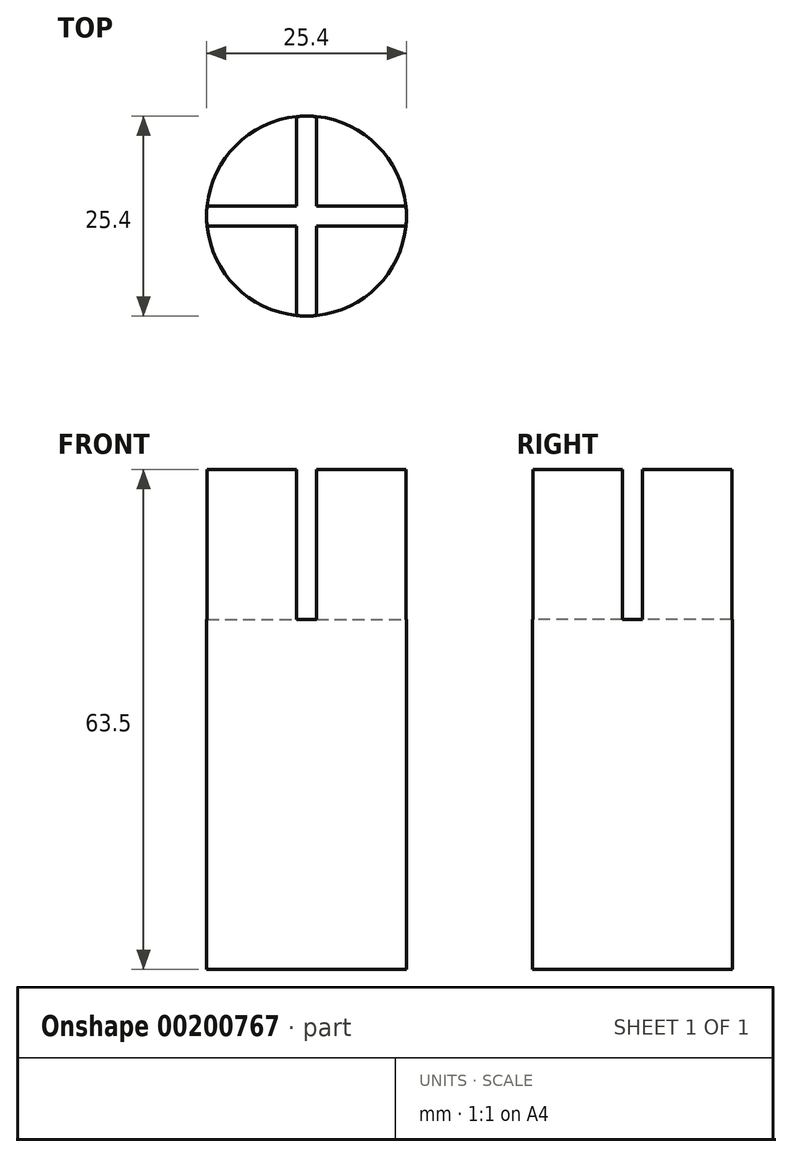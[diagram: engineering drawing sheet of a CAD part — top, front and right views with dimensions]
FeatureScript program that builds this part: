
annotation { "Feature Type Name" : "Feature", "Feature Type Description" : "" }
export const myFeature = defineFeature(function(context is Context, id is Id, definition is map)
    precondition{}
    {
        {
            var Q0;
            Q0=qCreatedBy(makeId("Top.planeOp"),FACE);
            var sketch = newSketch(context, id + "F0", { "sketchPlane" : qUnion([Q0])});
            skCircle(sketch, "E0", {"center": v(0, 0) * mm, "radius": 12.7 * mm});
            skSolve(sketch);
        }
        {
            var Q0;
            Q0 = qSketchRegion(id + "F0", true);
            extrude(context, id + "F1", {"entities" : qUnion([Q0]), "depth" : 63.5 * mm});
        }
        {
            var Q0;
            Q0=makeQuery(id+"F1.opExtrude","CAP_FACE",FACE,{"disambiguationData":[OSD([sQuery(id+"F0.wireOp",EDGE,"E0")])],"isStart":false});
            var sketch = newSketch(context, id + "F2", { "sketchPlane" : qUnion([Q0])});
            skLineSegment(sketch, "E1.bottom", {"start": v(-1.27, 12.7) * mm, "end": v(1.27, 12.7) * mm});
            skLineSegment(sketch, "E1.top", {"start": v(-1.27, -12.7) * mm, "end": v(1.27, -12.7) * mm});
            skLineSegment(sketch, "E1.left", {"start": v(-1.27, 12.7) * mm, "end": v(-1.27, -12.7) * mm});
            skLineSegment(sketch, "E1.right", {"start": v(1.27, 12.7) * mm, "end": v(1.27, -12.7) * mm});
            skPoint(sketch, "E1.middle", {"position": v(0, 0) * mm});
            skLineSegment(sketch, "E2.bottom", {"start": v(-12.7, 1.27) * mm, "end": v(12.7, 1.27) * mm});
            skLineSegment(sketch, "E2.top", {"start": v(-12.7, -1.27) * mm, "end": v(12.7, -1.27) * mm});
            skLineSegment(sketch, "E2.left", {"start": v(-12.7, 1.27) * mm, "end": v(-12.7, -1.27) * mm});
            skLineSegment(sketch, "E2.right", {"start": v(12.7, 1.27) * mm, "end": v(12.7, -1.27) * mm});
            skSolve(sketch);
        }
        {
            var Q0;
            Q0 = qSketchRegion(id + "F2", true);
            extrude(context, id + "F3", {"entities" : qUnion([Q0]), "operationType" : NewBodyOperationType.REMOVE, "oppositeDirection" : true, "depth" : 19.05 * mm});
        }
    });
